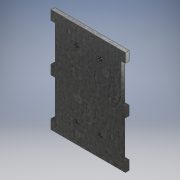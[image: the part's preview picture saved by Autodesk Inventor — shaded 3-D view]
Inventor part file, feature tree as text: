
AUTODESK INVENTOR PART (.ipt)
format: ipt  version: 2017 (Build 210142000, 142)  size: 161,792 bytes
history: native  units: mm
features: other x1, extrude x1, sketch x1
ambient origin geometry x8: Origin, YZ Plane, XZ Plane, XY Plane, X Axis, Y Axis, Z Axis, Center Point
bodies: Body1 (feature_tree)
feature tree (3):
  other  "Sólido1"
  extrude  "Extrusión1"  Depth=139.7mm
  sketch  "Boceto1"  dims[d0=88.9mm d1=139.7mm d2=7.9375mm d3=7.9375mm d4=7.9375mm d5=7.9375mm d6=88.9mm d7=28.575mm d8=28.575mm d9=28.575mm d10=28.575mm d11=25.4mm d12=25.4mm d13=88.9mm d14=5.0mm d15=0.0mm d17=5.55625mm d18=12.7mm d19=5.55625mm d20=12.7mm d21=5.55625mm d22=12.7mm d23=5.55625mm d24=12.7mm d25=5.55625mm d26=12.7mm d27=5.55625mm d28=12.7mm d29=63.5mm d30=63.5mm]
